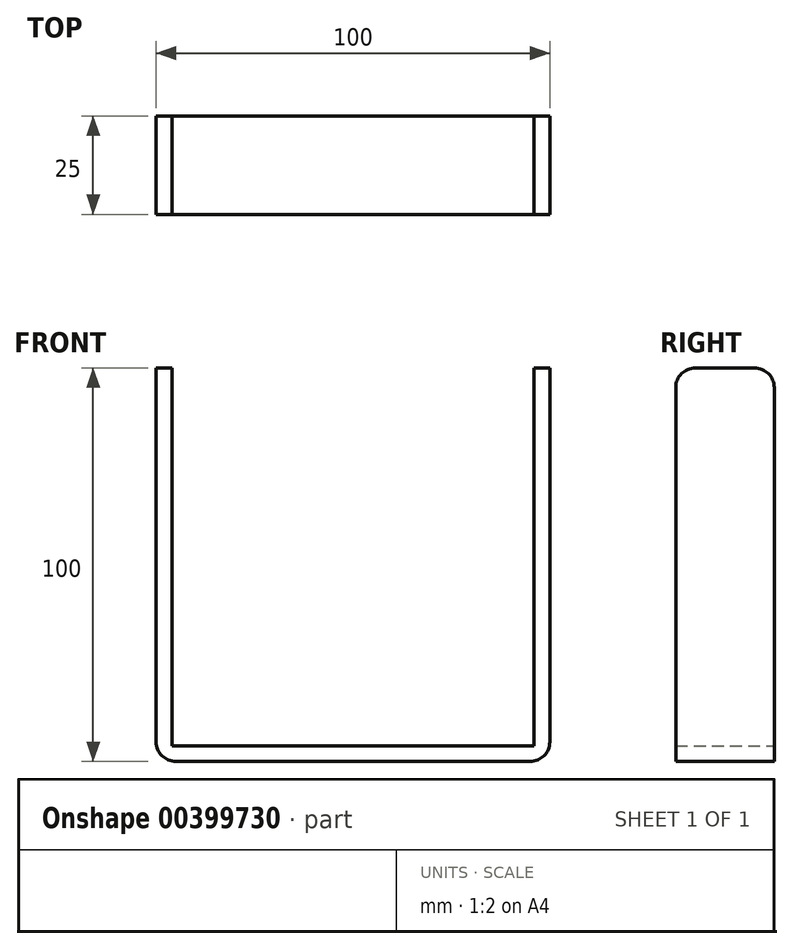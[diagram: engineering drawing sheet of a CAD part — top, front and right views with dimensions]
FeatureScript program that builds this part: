
annotation { "Feature Type Name" : "Feature", "Feature Type Description" : "" }
export const myFeature = defineFeature(function(context is Context, id is Id, definition is map)
    precondition{}
    {
        {
            var Q0;
            Q0=qCreatedBy(makeId("Front.planeOp"),FACE);
            var sketch = newSketch(context, id + "F0", { "sketchPlane" : qUnion([Q0])});
            skLineSegment(sketch, "E0", {"start": v(-53.1, 66.8) * mm, "end": v(-53.1, -33.2) * mm});
            skLineSegment(sketch, "E1", {"start": v(-53.1, -33.2) * mm, "end": v(46.9, -33.2) * mm});
            skLineSegment(sketch, "E2.1", {"start": v(-49.1, 66.8) * mm, "end": v(-49.1, -29.2) * mm});
            skLineSegment(sketch, "E3", {"start": v(-53.1, 66.8) * mm, "end": v(-49.1, 66.8) * mm});
            skLineSegment(sketch, "E4", {"start": v(46.9, 66.8) * mm, "end": v(42.9, 66.8) * mm});
            skLineSegment(sketch, "E5", {"start": v(42.9, 66.8) * mm, "end": v(42.9, -29.2) * mm});
            skLineSegment(sketch, "E6", {"start": v(-49.1, -29.2) * mm, "end": v(42.9, -29.2) * mm});
            skLineSegment(sketch, "E7", {"start": v(46.9, 66.8) * mm, "end": v(46.9, -33.2) * mm});
            skSolve(sketch);
        }
        {
            var Q0;
            Q0=makeQuery(id+"F0.imprint","IMPRINT",FACE,{"disambiguationData":[TD([[makeQuery(id+"F0.imprint","IMPRINT",EDGE,{"derivedFrom":sQuery(id+"F0.wireOp",EDGE,"E0")}),1.0]])]});
            extrude(context, id + "F1", {"entities" : qUnion([Q0]), "endBound" : BoundingType.SYMMETRIC, "depth" : 25 * mm});
        }
        {
            var Q0;
            Q0=makeQuery(id+"F1.opExtrude","CAP_EDGE",EDGE,{"disambiguationData":[OSD([sQuery(id+"F0.wireOp",EDGE,"E3")])],"isStart":false});
            var Q1;
            Q1=makeQuery(id+"F1.opExtrude","CAP_EDGE",EDGE,{"disambiguationData":[OSD([sQuery(id+"F0.wireOp",EDGE,"E3")])],"isStart":true});
            var Q2;
            Q2=makeQuery(id+"F1.opExtrude","CAP_EDGE",EDGE,{"disambiguationData":[OSD([sQuery(id+"F0.wireOp",EDGE,"1UERXiUU-1GoZ-Fz5K-BldK-O9Ez4MNL6dWU")])],"isStart":false});
            var Q3;
            Q3=makeQuery(id+"F1.opExtrude","CAP_EDGE",EDGE,{"disambiguationData":[OSD([sQuery(id+"F0.wireOp",EDGE,"1UERXiUU-1GoZ-Fz5K-BldK-O9Ez4MNL6dWU")])],"isStart":true});
            var Q4;
            Q4=makeQuery(id+"F1.opExtrude","CAP_EDGE",EDGE,{"disambiguationData":[OSD([sQuery(id+"F0.wireOp",EDGE,"E4")])],"isStart":false});
            var Q5;
            Q5=makeQuery(id+"F1.opExtrude","CAP_EDGE",EDGE,{"disambiguationData":[OSD([sQuery(id+"F0.wireOp",EDGE,"E4")])],"isStart":true});
            var Q6;
            Q6=makeQuery(id+"F1.opExtrude","SWEPT_EDGE",EDGE,{"disambiguationData":[OSD([sQuery(id+"F0.wireOp",EDGE,"E1"),sQuery(id+"F0.wireOp",EDGE,"E7")])]});
            var Q7;
            Q7=makeQuery(id+"F1.opExtrude","SWEPT_EDGE",EDGE,{"disambiguationData":[OSD([sQuery(id+"F0.wireOp",EDGE,"E0"),sQuery(id+"F0.wireOp",EDGE,"E1")])]});
            fillet(context, id + "F2", {"entities" : qUnion([Q0, Q1, Q2, Q3, Q4, Q5, Q6, Q7]), "radius" : 5 * mm, "tangentPropagation" : true, "allowEdgeOverflow" : false});
        }
    });
